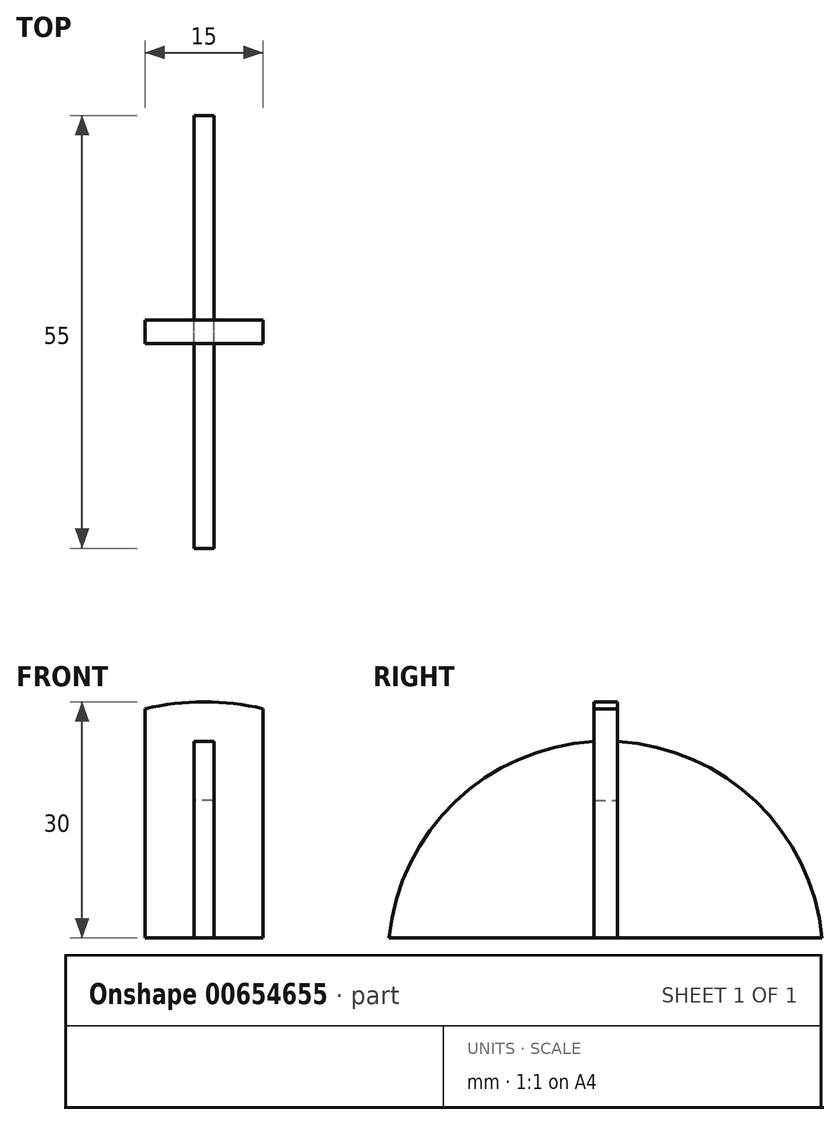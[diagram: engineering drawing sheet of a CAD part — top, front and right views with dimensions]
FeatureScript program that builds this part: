
annotation { "Feature Type Name" : "Feature", "Feature Type Description" : "" }
export const myFeature = defineFeature(function(context is Context, id is Id, definition is map)
    precondition{}
    {
        {
            var Q0;
            Q0=qCreatedBy(makeId("Front.planeOp"),FACE);
            var sketch = newSketch(context, id + "F0", { "sketchPlane" : qUnion([Q0])});
            skLineSegment(sketch, "E0", {"start": v(-32.5, 0) * mm, "end": v(32.5, 0) * mm});
            skLineSegment(sketch, "E1", {"start": v(0, 0) * mm, "end": v(0, 30) * mm});
            skArc(sketch, "E2", {"start": v(32.5, 0) * mm, "mid": v(0, 30) * mm, "end": v(-32.5, 0) * mm});
            skLineSegment(sketch, "E3.bottom", {"start": v(7.5, 0) * mm, "end": v(-7.5, 0) * mm});
            skLineSegment(sketch, "E3.top", {"start": v(7.5, 60) * mm, "end": v(-7.5, 60) * mm});
            skLineSegment(sketch, "E3.left", {"start": v(7.5, 0) * mm, "end": v(7.5, 60) * mm});
            skLineSegment(sketch, "E3.right", {"start": v(-7.5, 0) * mm, "end": v(-7.5, 60) * mm});
            skPoint(sketch, "E3.middle", {"position": v(0, 30) * mm});
            skLineSegment(sketch, "E4.bottom", {"start": v(-1.25, 0) * mm, "end": v(1.25, 0) * mm});
            skLineSegment(sketch, "E4.top", {"start": v(-1.25, 17.5) * mm, "end": v(1.25, 17.5) * mm});
            skLineSegment(sketch, "E4.left", {"start": v(-1.25, 0) * mm, "end": v(-1.25, 17.5) * mm});
            skLineSegment(sketch, "E4.right", {"start": v(1.25, 0) * mm, "end": v(1.25, 17.5) * mm});
            skLineSegment(sketch, "E5.bottom", {"start": v(-7.5, 60) * mm, "end": v(7.5, 60) * mm});
            skLineSegment(sketch, "E5.top", {"start": v(-7.5, 72.5) * mm, "end": v(7.5, 72.5) * mm});
            skLineSegment(sketch, "E5.left", {"start": v(-7.5, 60) * mm, "end": v(-7.5, 72.5) * mm});
            skLineSegment(sketch, "E5.right", {"start": v(7.5, 60) * mm, "end": v(7.5, 72.5) * mm});
            skLineSegment(sketch, "E6.bottom", {"start": v(0.25, 60) * mm, "end": v(-0.25, 60) * mm});
            skLineSegment(sketch, "E6.top", {"start": v(0.25, 85) * mm, "end": v(-0.25, 85) * mm});
            skLineSegment(sketch, "E6.left", {"start": v(0.25, 60) * mm, "end": v(0.25, 85) * mm});
            skLineSegment(sketch, "E6.right", {"start": v(-0.25, 60) * mm, "end": v(-0.25, 85) * mm});
            skPoint(sketch, "E6.middle", {"position": v(0, 72.5) * mm});
            skSolve(sketch);
        }
        {
            var Q0;
            {var subQ0=sQuery(id+"F0.wireOp",EDGE,"E5.bottom");Q0=makeQuery(id+"F0.imprint","IMPRINT",FACE,{"disambiguationData":[TD([[makeQuery(id+"F0.imprint","IMPRINT",EDGE,{"derivedFrom":subQ0}),-1.0]])]});}
            var Q1;
            {var subQ5=sQuery(id+"F0.wireOp",EDGE,"E4.left");Q1=makeQuery(id+"F0.imprint","IMPRINT",FACE,{"disambiguationData":[TD([[makeQuery(id+"F0.imprint","IMPRINT",EDGE,{"derivedFrom":subQ5}),1.0]])]});}
            var Q2;
            Q2=makeQuery(id+"F0.imprint","IMPRINT",FACE,{"disambiguationData":[TD([[makeQuery(id+"F0.imprint","IMPRINT",EDGE,{"derivedFrom":sQuery(id+"F0.wireOp",EDGE,"E5.bottom")}),1.0]])]});
            var Q3;
            {var subQ7=sQuery(id+"F0.wireOp",EDGE,"E4.right");Q3=makeQuery(id+"F0.imprint","IMPRINT",FACE,{"disambiguationData":[TD([[makeQuery(id+"F0.imprint","IMPRINT",EDGE,{"derivedFrom":subQ7}),-1.0]])]});}
            var Q4;
            {var subQ0=sQuery(id+"F0.wireOp",EDGE,"E2");var subQ1=sQuery(id+"F0.wireOp",EDGE,"E0");var subQ2=makeQuery(id+"F0.imprint","INTERSECT",VERTEX,{"disambiguationData":[OD(1.0)],"derivedFrom":[subQ1,subQ0]});Q4=makeQuery(id+"F0.imprint","IMPRINT",FACE,{"disambiguationData":[TD([[makeQuery(id+"F0.imprint","IMPRINT",EDGE,{"disambiguationData":[TD([[subQ2,-1.0]])],"derivedFrom":subQ0}),1.0]])]});}
            var Q5;
            {var subQ0=sQuery(id+"F0.wireOp",EDGE,"E2");var subQ1=sQuery(id+"F0.wireOp",EDGE,"E0");var subQ2=makeQuery(id+"F0.imprint","INTERSECT",VERTEX,{"disambiguationData":[OD(0.0)],"derivedFrom":[subQ1,subQ0]});Q5=makeQuery(id+"F0.imprint","IMPRINT",FACE,{"disambiguationData":[TD([[makeQuery(id+"F0.imprint","IMPRINT",EDGE,{"disambiguationData":[TD([[subQ2,1.0]])],"derivedFrom":subQ0}),1.0]])]});}
            extrude(context, id + "F1", {"entities" : qUnion([Q0, Q1, Q2, Q3, Q4, Q5]), "depth" : 3 * mm, "offsetDistance" : 25 * mm});
        }
        {
            var Q0;
            Q0=makeQuery(id+"F1.opExtrude","SWEPT_FACE",FACE,{"disambiguationData":[OSD([sQuery(id+"F0.wireOp",EDGE,"E4.left")])]});
            var sketch = newSketch(context, id + "F2", { "sketchPlane" : qUnion([Q0])});
            skLineSegment(sketch, "E7.0", {"start": v(-3, 0) * mm, "end": v(-3, 17.5) * mm});
            skLineSegment(sketch, "E8.0", {"start": v(0, 0) * mm, "end": v(0, 17.5) * mm});
            skLineSegment(sketch, "E9.0", {"start": v(-3, 17.5) * mm, "end": v(0, 17.5) * mm});
            skLineSegment(sketch, "E10.0", {"start": v(-3, 0) * mm, "end": v(0, 0) * mm});
            skLineSegment(sketch, "E11", {"start": v(-1.5, 0) * mm, "end": v(26, 0) * mm});
            skLineSegment(sketch, "E12", {"start": v(26, 0) * mm, "end": v(-29, 0) * mm});
            skPoint(sketch, "E13", {"position": v(-1.5, 25) * mm});
            skArc(sketch, "E14", {"start": v(26, 0) * mm, "mid": v(-1.5, 25) * mm, "end": v(-29, 0) * mm});
            skLineSegment(sketch, "E15", {"start": v(-3, 17.5) * mm, "end": v(-3, 24.96) * mm});
            skLineSegment(sketch, "E16", {"start": v(0, 17.5) * mm, "end": v(0, 24.96) * mm});
            skSolve(sketch);
        }
        {
            var Q0;
            {var subQ0=sQuery(id+"F2.wireOp",EDGE,"E7.0");Q0=makeQuery(id+"F2.imprint","IMPRINT",FACE,{"disambiguationData":[TD([[makeQuery(id+"F2.imprint","IMPRINT",EDGE,{"derivedFrom":subQ0}),-1.0]])]});}
            var Q1;
            {var subQ0=sQuery(id+"F2.wireOp",EDGE,"E7.0");Q1=makeQuery(id+"F2.imprint","IMPRINT",FACE,{"disambiguationData":[TD([[makeQuery(id+"F2.imprint","IMPRINT",EDGE,{"derivedFrom":subQ0}),1.0]])]});}
            var Q2;
            {var subQ0=sQuery(id+"F2.wireOp",EDGE,"E8.0");Q2=makeQuery(id+"F2.imprint","IMPRINT",FACE,{"disambiguationData":[TD([[makeQuery(id+"F2.imprint","IMPRINT",EDGE,{"derivedFrom":subQ0}),-1.0]])]});}
            extrude(context, id + "F3", {"entities" : qUnion([Q0, Q1, Q2]), "depth" : 2.5 * mm, "offsetDistance" : 25 * mm});
        }
    });
